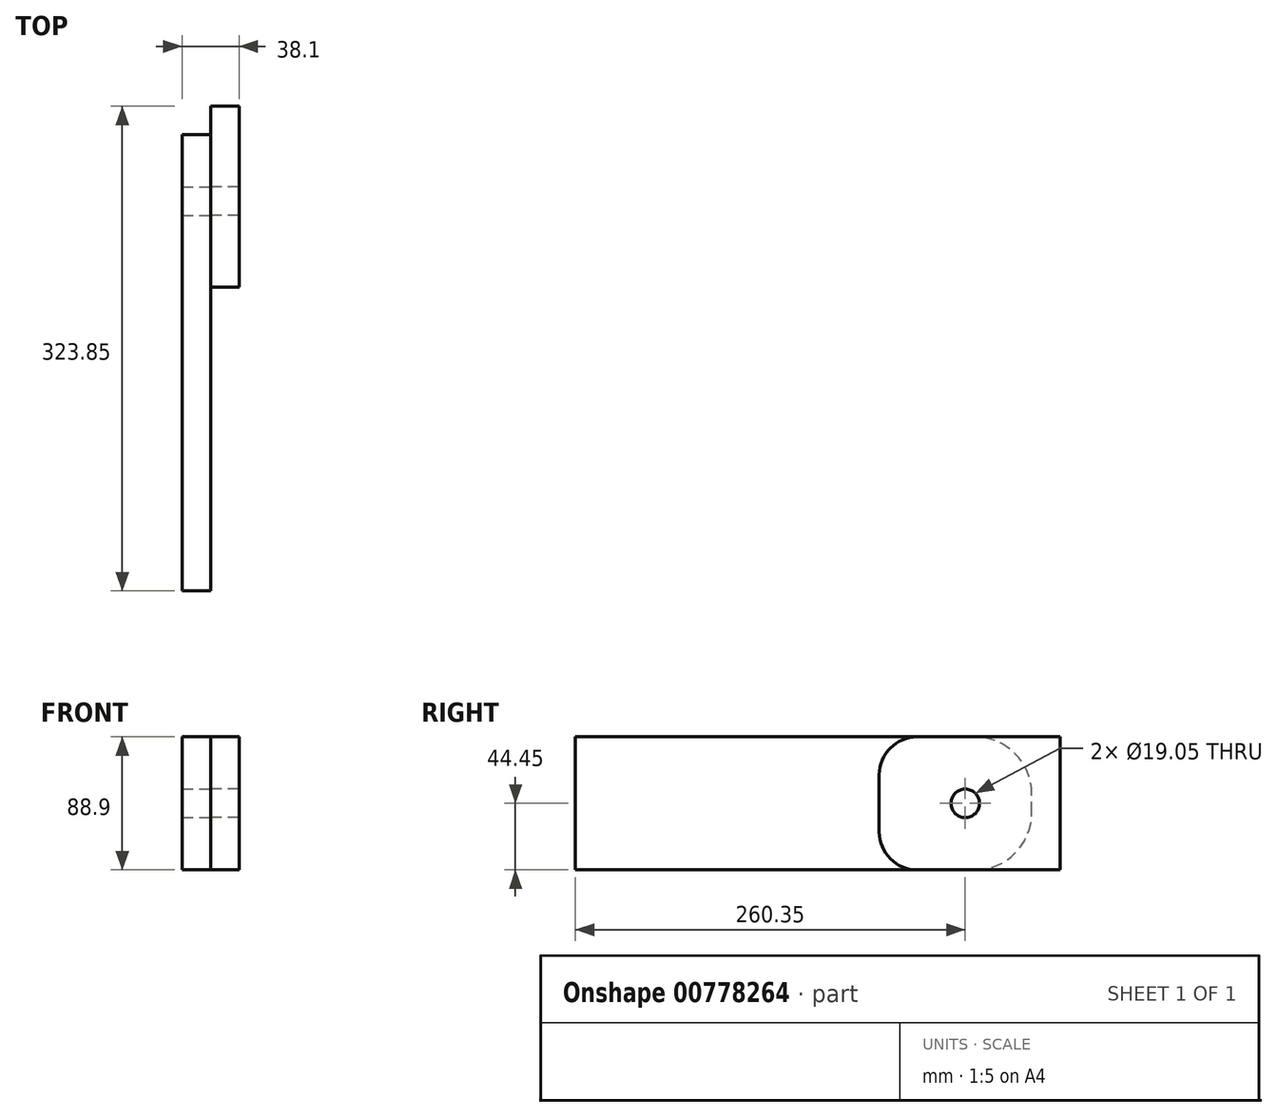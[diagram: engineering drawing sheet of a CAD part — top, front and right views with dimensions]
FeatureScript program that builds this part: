
annotation { "Feature Type Name" : "Feature", "Feature Type Description" : "" }
export const myFeature = defineFeature(function(context is Context, id is Id, definition is map)
    precondition{}
    {
        {
            var Q0;
            Q0=qCreatedBy(makeId("Right.planeOp"),FACE);
            var sketch = newSketch(context, id + "F0", { "sketchPlane" : qUnion([Q0])});
            skLineSegment(sketch, "E0.bottom", {"start": v(0, 0) * mm, "end": v(304.8, 0) * mm});
            skLineSegment(sketch, "E0.top", {"start": v(0, 88.9) * mm, "end": v(304.8, 88.9) * mm});
            skLineSegment(sketch, "E0.left", {"start": v(0, 0) * mm, "end": v(0, 88.9) * mm});
            skLineSegment(sketch, "E0.right", {"start": v(304.8, 0) * mm, "end": v(304.8, 88.9) * mm});
            skSolve(sketch);
        }
        {
            var Q0;
            Q0 = qSketchRegion(id + "F0", true);
            extrude(context, id + "F1", {"entities" : qUnion([Q0]), "depth" : 19.05 * mm, "offsetDistance" : 25.4 * mm});
        }
        {
            var Q0;
            Q0=makeQuery(id+"F1.opExtrude","SWEPT_EDGE",EDGE,{"disambiguationData":[OSD([sQuery(id+"F0.wireOp",EDGE,"E0.top"),sQuery(id+"F0.wireOp",EDGE,"E0.right")])]});
            var Q1;
            Q1=makeQuery(id+"F1.opExtrude","SWEPT_EDGE",EDGE,{"disambiguationData":[OSD([sQuery(id+"F0.wireOp",EDGE,"E0.bottom"),sQuery(id+"F0.wireOp",EDGE,"E0.right")])]});
            fillet(context, id + "F2", {"entities" : qUnion([Q0, Q1]), "radius" : 38.1 * mm, "tangentPropagation" : true, "allowEdgeOverflow" : false});
        }
        {
            var Q0;
            Q0=makeQuery(id+"F1.opExtrude","CAP_FACE",FACE,{"disambiguationData":[OSD([sQuery(id+"F0.wireOp",EDGE,"E0.bottom"),sQuery(id+"F0.wireOp",EDGE,"E0.top"),sQuery(id+"F0.wireOp",EDGE,"E0.left"),sQuery(id+"F0.wireOp",EDGE,"E0.right")])],"isStart":false});
            var sketch = newSketch(context, id + "F3", { "sketchPlane" : qUnion([Q0])});
            skCircle(sketch, "E1", {"center": v(260.35, 44.45) * mm, "radius": 9.53 * mm});
            skSolve(sketch);
        }
        {
            var Q0;
            Q0 = qSketchRegion(id + "F3", true);
            extrude(context, id + "F4", {"entities" : qUnion([Q0]), "operationType" : NewBodyOperationType.REMOVE, "endBound" : BoundingType.THROUGH_ALL, "oppositeDirection" : true, "depth" : 25.4 * mm, "offsetDistance" : 25.4 * mm});
        }
        {
            var Q0;
            Q0=makeQuery(id+"F1.opExtrude","CAP_FACE",FACE,{"disambiguationData":[OSD([sQuery(id+"F0.wireOp",EDGE,"E0.bottom"),sQuery(id+"F0.wireOp",EDGE,"E0.top"),sQuery(id+"F0.wireOp",EDGE,"E0.left"),sQuery(id+"F0.wireOp",EDGE,"E0.right")])],"isStart":false});
            var sketch = newSketch(context, id + "F5", { "sketchPlane" : qUnion([Q0])});
            skLineSegment(sketch, "E2.0", {"start": v(228.3, 88.9) * mm, "end": v(266.7, 88.9) * mm});
            skArc(sketch, "E3.0", {"start": v(304.8, 50.8) * mm, "mid": v(293.64, 77.74) * mm, "end": v(266.7, 88.9) * mm});
            skLineSegment(sketch, "E4.0", {"start": v(304.8, 38.1) * mm, "end": v(304.8, 50.8) * mm});
            skArc(sketch, "E5.0", {"start": v(266.7, 0) * mm, "mid": v(293.64, 11.16) * mm, "end": v(304.8, 38.1) * mm});
            skLineSegment(sketch, "E6.0", {"start": v(228.3, 0) * mm, "end": v(266.7, 0) * mm});
            skCircle(sketch, "E7.0", {"center": v(260.35, 44.45) * mm, "radius": 9.53 * mm});
            skLineSegment(sketch, "E8", {"start": v(202.9, 63.5) * mm, "end": v(202.9, 25.4) * mm});
            skLineSegment(sketch, "E9", {"start": v(202.9, 0) * mm, "end": v(202.9, 88.9) * mm});
            skPoint(sketch, "E10.newPointA", {"position": v(0, 88.9) * mm});
            skArc(sketch, "E10.filletArc", {"start": v(228.3, 88.9) * mm, "mid": v(210.33, 81.46) * mm, "end": v(202.9, 63.5) * mm});
            skPoint(sketch, "E11.newPointA", {"position": v(202.9, 0) * mm});
            skPoint(sketch, "E11.newPointB", {"position": v(0, 0) * mm});
            skArc(sketch, "E11.filletArc", {"start": v(202.9, 25.4) * mm, "mid": v(210.33, 7.44) * mm, "end": v(228.3, 0) * mm});
            skLineSegment(sketch, "E12", {"start": v(228.3, 88.9) * mm, "end": v(323.85, 88.9) * mm});
            skLineSegment(sketch, "E13", {"start": v(323.85, 88.9) * mm, "end": v(323.85, 0) * mm});
            skLineSegment(sketch, "E14", {"start": v(323.85, 0) * mm, "end": v(228.3, 0) * mm});
            skSolve(sketch);
        }
        {
            var Q0;
            Q0 = qSketchRegion(id + "F5", true);
            extrude(context, id + "F6", {"entities" : qUnion([Q0]), "depth" : 19.05 * mm, "offsetDistance" : 25.4 * mm});
        }
    });
